# Revit family: НЕBАТОМ_Переходный патрубок VO, Версия 1
name_source: partatom
category: Оборудование
revit_build: Autodesk Revit 2017 (Build: 20170118_1100(x64)
units: mm (PartAtom-declared; Revit-internal decimal feet)

## family parameters
Всегда вертикально = Нет
На основе рабочей плоскости = Нет
Общий = Нет
При загрузке вырезать с полостями = Нет
Размер круглого соединителя = Использовать диаметр
Тип детали = Нормальный
Точка расчета площади = Нет

## types (11) — shared parameters
ADSK_Единица измерения = шт.
ADSK_Завод-изготовитель = НЕВАТОМ
ADSK_Количество = 1
ADSK_Материал наименование = сталь оцинкованная
ADSK_Наименование = Переходный патрубок
L = 150 мм
Nevatom_URL = https://t.me
толщина стенки = 5 мм

## per-type parameters (varying)
| type | ADSK_Марка | ADSK_Масса | D | D внешний | D внутренний | D1 | Dнв | Dнф |
| Переходный патрубок VO №4,0 | VO-400 | 7.3 | 400 мм | 410 мм | 400 мм | 400 мм | 480 мм | 450 мм |
| Переходный патрубок VO №4,5 | VO-450 | 9.9 | 450 мм | 460 мм | 450 мм | 450 мм | 530 мм | 500 мм |
| Переходный патрубок VO №5,0 | VO-500 | 11.3 | 500 мм | 510 мм | 500 мм | 500 мм | 590 мм | 550 мм |
| Переходный патрубок VO №5,6 | VO-560 | 13.9 | 560 мм | 570 мм | 560 мм | 560 мм | 650 мм | 610 мм |
| Переходный патрубок VO №6,3 | VO-630 | 14.5 | 630 мм | 640 мм | 630 мм | 630 мм | 730 мм | 680 мм |
| Переходный патрубок VO №7,1 | VO-710 | 21 | 710 мм | 720 мм | 710 мм | 710 мм | 810 мм | 790 мм |
| Переходный патрубок VO №8,0 | VO-800 | 23 | 800 мм | 810 мм | 800 мм | 800 мм | 900 мм | 864 мм |
| Переходный патрубок VO №9,0 | VO-900 | 27.1 | 900 мм | 910 мм | 900 мм | 900 мм | 1010 мм | 964 мм |
| Переходный патрубок VO №10,0 | VO-1000 | 30.5 | 1000 мм | 1010 мм | 1000 мм | 1000 мм | 1100 мм | 1080 мм |
| Переходный патрубок VO №11,2 | VO-1120 | 36.2 | 1120 мм | 1130 мм | 1120 мм | 1120 мм | 1230 мм | 1184 мм |
| Переходный патрубок VO №12,5 | VO-1250 | 41.9 | 1250 мм | 1260 мм | 1250 мм | 1250 мм | 1360 мм | 1330 мм |
